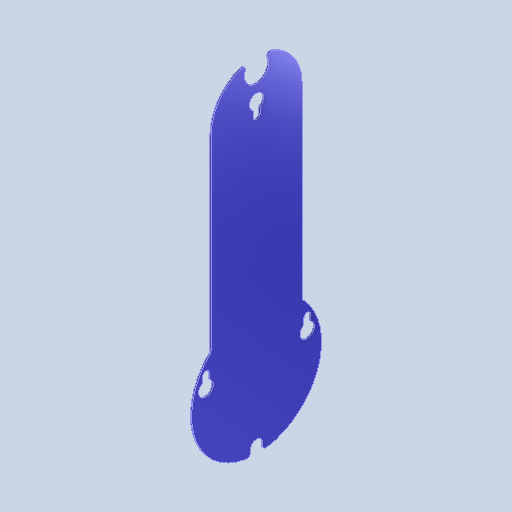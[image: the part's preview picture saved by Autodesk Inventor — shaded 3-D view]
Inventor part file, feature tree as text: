
AUTODESK INVENTOR PART (.ipt)
format: ipt  version: 2024.2 (Build 282272000, 272)  size: 412,160 bytes
history: native  units: mm
features: other x4, sketch x2, extrude x1
ambient origin geometry x8: Origin, YZ Plane, XZ Plane, XY Plane, X Axis, Y Axis, Z Axis, Center Point
bodies: Solid1 (feature_tree)
feature tree (7):
  other  "LowerArmFrame.ipt"
  extrude  "Extrusion1"  Depth=4.0mm
  other  "TaggingFeature1"
  sketch  "Sketch1"  dims[d0=10.0mm]
  sketch  "Sketch1_1"  dims[d2=20.0mm d4=20.0mm d6=30.0mm d8=10.0mm d9=3.0mm d10=5.5mm d11=5.5mm d12=20.0mm d13=20.0mm d14=1.0mm d15=1.0mm d16=23.947282mm d17=23.947282mm d18=23.947282mm d20=10.0mm d22=1.396263mm d23=140.0mm d24=0.75mm d25=0.0mm d26=15.0mm d27=2.0mm d28=9.0mm d29=6.0mm d30=4.0mm d31=0.1mm d32=15.0mm d36=9.0mm d37=4.0mm d38=6.0mm d39=0.1mm]
  other  "Solid1::LowerArmFrame.ipt"
  other  "Srf1"
